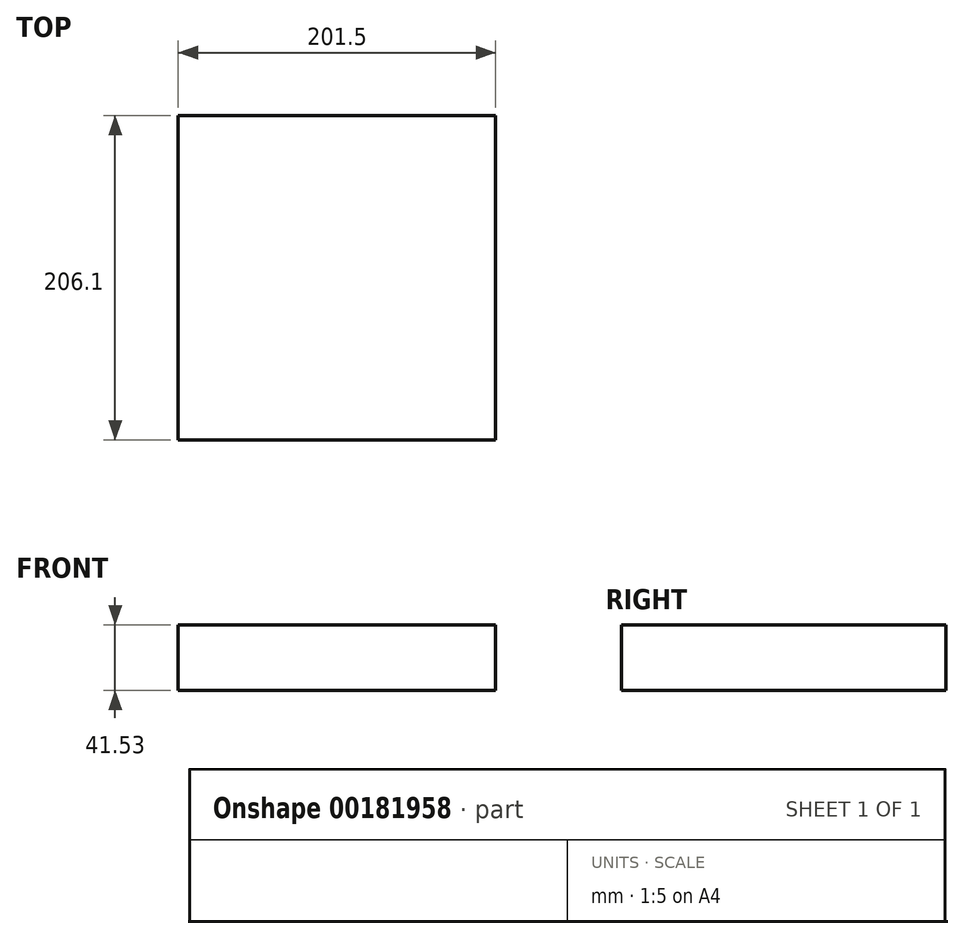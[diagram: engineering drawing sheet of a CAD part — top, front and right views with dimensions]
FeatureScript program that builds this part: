
annotation { "Feature Type Name" : "Feature", "Feature Type Description" : "" }
export const myFeature = defineFeature(function(context is Context, id is Id, definition is map)
    precondition{}
    {
        {
            var Q0;
            Q0=qCreatedBy(makeId("Top.planeOp"),FACE);
            var sketch = newSketch(context, id + "F0", { "sketchPlane" : qUnion([Q0])});
            skLineSegment(sketch, "E0.bottom", {"start": v(100.75, 103.05) * mm, "end": v(-100.75, 103.05) * mm});
            skLineSegment(sketch, "E0.top", {"start": v(100.75, -103.05) * mm, "end": v(-100.75, -103.05) * mm});
            skLineSegment(sketch, "E0.left", {"start": v(100.75, 103.05) * mm, "end": v(100.75, -103.05) * mm});
            skLineSegment(sketch, "E0.right", {"start": v(-100.75, 103.05) * mm, "end": v(-100.75, -103.05) * mm});
            skPoint(sketch, "E0.middle", {"position": v(0, 0) * mm});
            skSolve(sketch);
        }
        {
            var Q0;
            Q0=makeQuery(id+"F0.imprint","IMPRINT",FACE,{"disambiguationData":[TD([[makeQuery(id+"F0.imprint","IMPRINT",EDGE,{"derivedFrom":sQuery(id+"F0.wireOp",EDGE,"E0.bottom")}),1.0]])]});
            extrude(context, id + "F1", {"entities" : qUnion([Q0]), "depth" : 41.53 * mm});
        }
    });
